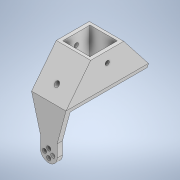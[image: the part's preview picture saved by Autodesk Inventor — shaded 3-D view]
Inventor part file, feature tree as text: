
AUTODESK INVENTOR PART (.ipt)
format: ipt  version: 2022 (Build 260153000, 153)  size: 187,392 bytes
history: native  units: mm
features: extrude x8, sketch x8, plane x1
ambient origin geometry x8: Origin, YZ Plane, XZ Plane, XY Plane, X Axis, Y Axis, Z Axis, Center Point
bodies: Solid1 (feature_tree)
feature tree (17):
  extrude  "Extrusion1"  Depth=4.0mm TaperAngle=360.0deg
  extrude  "Extrusion2"  Depth=5.0mm
  extrude  "Extrusion4"  Depth=73.5mm TaperAngle=0.0deg
  extrude  "Extrusion5"  Depth=12.7mm
  extrude  "Extrusion6"  Depth=3.0mm
  extrude  "Extrusion7"  Depth=3.0mm TaperAngle=0.0deg
  plane  "Work Plane1"
  extrude  "Extrusion8"  Depth=26.0mm
  extrude  "Extrusion9"  Depth=25.4mm TaperAngle=0.0deg
  sketch  "Sketch1"  dims[d2=4.0mm d3=40.0mm d5=360.0deg]
  sketch  "Sketch2"  dims[d16=5.0mm d17=0.0mm d18=13.25mm]
  sketch  "Sketch4"  dims[d19=2.0mm d20=0.0mm d26=73.5mm d27=0.0mm]
  sketch  "Sketch5"  dims[d28=30.0mm d29=0.0mm d30=12.7mm]
  sketch  "Sketch6"  dims[d31=12.7mm d32=3.0mm]
  sketch  "Sketch7"  dims[d33=3.0mm d34=30.0mm d35=0.0mm]
  sketch  "Sketch8"  dims[d37=13.0mm d38=26.0mm]
  sketch  "Sketch9"  dims[d39=26.0mm d40=25.4mm d41=0.0mm d43=4.0mm d44=0.0mm d45=0.0mm d47=4.0mm d48=10.0mm d49=0.0mm]
